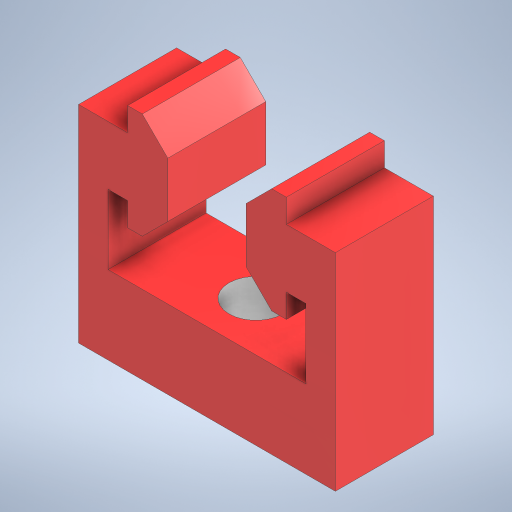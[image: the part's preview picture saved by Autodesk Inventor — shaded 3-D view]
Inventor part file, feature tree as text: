
AUTODESK INVENTOR PART (.ipt)
format: ipt  version: 2023.2 (Build 272271030, 271C)  size: 293,888 bytes
history: native  units: mm
features: extrude x2, sketch x2, plane x1
ambient origin geometry x8: Origin, YZ Plane, XZ Plane, XY Plane, X Axis, Y Axis, Z Axis, Center Point
bodies: Solid1 (feature_tree)
feature tree (5):
  extrude  "Extrusion1"  Depth=3.0mm
  plane  "Work Plane1"
  sketch  "Sketch2"  dims[d14=0.1mm d17=0.1mm d18=0.09mm d19=10.0mm d20=0.0mm d21=-7.8mm d22=5.5mm d27=0.0mm d28=0.0mm d31=8.0mm]
  extrude  "Extrusion3"  Depth=8.0mm
  sketch  "Sketch1"  dims[d0=20.0mm d1=20.0mm d2=5.0mm d3=6.1mm d4=6.1mm d5=1.5mm d6=4.5mm d7=4.5mm d8=1.5mm d9=6.9mm d10=1.8mm d13=3.0mm]
